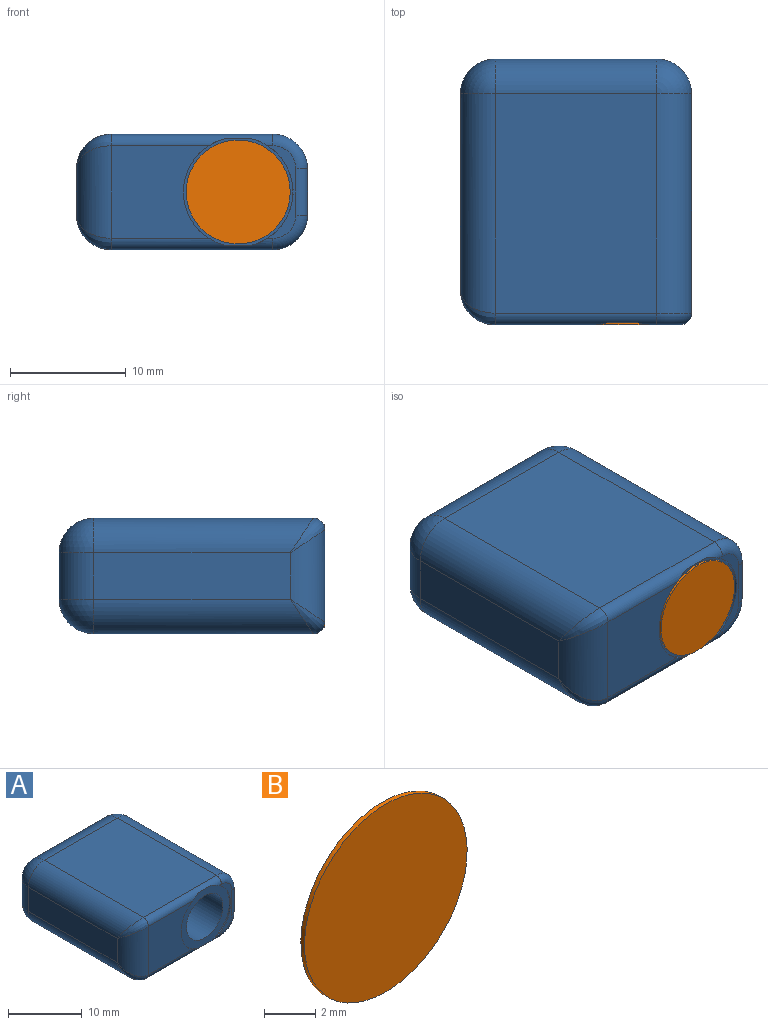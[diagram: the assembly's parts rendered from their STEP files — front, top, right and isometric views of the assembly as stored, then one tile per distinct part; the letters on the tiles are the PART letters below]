
ASSEMBLY  parts=2 mates=1
PART A: 34 faces, bbox 20.2x23x10.5 mm
  f0: cylinder r=4.75mm len=9.2mm, axis (0,-1,0), area 2.2mm2, adj f7,f9,f26,f30
  f1: plane 8.44x8mm, normal (0,-1,0), area 55.2mm2, adj f8,f23,f26,f30
  f2: plane 19x14mm, normal (0,0,1), area 266mm2, adj f15,f20,f24,f30
  f3: plane 17x4mm, normal (-1,0,0), area 68mm2, adj f19,f21,f23,f24
  f4: plane 19x14mm, normal (0,0,-1), area 266mm2, adj f12,f16,f21,f26
  f5: plane 19x4mm, normal (1,0,0), area 76mm2, adj f12,f14,f15,f28
  f6: plane 14x4mm, normal (0,1,0), area 48.9mm2, adj f14,f16,f19,f20,f32
  f7: plane 8x2.44mm, normal (0,-1,0), area 5.4mm2, adj f0,f26,f27,f28,f29,f30
  f8: cylinder r=4.75mm len=9.2mm, axis (0,-1,0), area 2.2mm2, adj f1,f9,f26,f30
  f9: plane 9.5x9.2mm, normal (0,-1,0), area 31.9mm2, adj f0,f8,f10,f26,f30
  f10: cylinder r=3.5mm len=10mm, axis (0,-1,0), area 219.9mm2, adj f9,f11
  f11: plane 7x7mm, normal (0,-1,0), area 38.5mm2, adj f10
  f12: cylinder r=3mm len=19mm, axis (0,1,0), area 89.5mm2, adj f4,f5,f13,f27
  f13: sphere r=3mm, area 14.1mm2, adj f12,f14,f16
  f14: cylinder r=3mm len=4mm, axis (0,0,-1), area 18.8mm2, adj f5,f6,f13,f17
  f15: cylinder r=3mm len=19mm, axis (0,-1,0), area 89.5mm2, adj f2,f5,f17,f29
  f16: cylinder r=3mm len=14mm, axis (-1,0,0), area 66mm2, adj f4,f6,f13,f18
  f17: sphere r=3mm, area 14.1mm2, adj f14,f15,f20
  f18: sphere r=3mm, area 14.1mm2, adj f16,f19,f21
  f19: cylinder r=3mm len=4mm, axis (0,0,1), area 18.8mm2, adj f3,f6,f18,f22
  f20: cylinder r=3mm len=14mm, axis (1,0,0), area 66mm2, adj f2,f6,f17,f22
  f21: cylinder r=3mm len=19mm, axis (0,-1,0), area 86.1mm2, adj f3,f4,f18,f25
  f22: sphere r=3mm, area 14.1mm2, adj f19,f20,f24
  f23: cylinder r=3mm len=8mm, axis (0,0,-1), area 30.8mm2, adj f1,f3,f25,f31
  f24: cylinder r=3mm len=19mm, axis (0,1,0), area 86.1mm2, adj f2,f3,f22,f31
  f25: bspline ~3.38x3mm, area 5mm2, adj f21,f23,f26
  f26: cylinder r=1mm len=14mm, axis (-1,0,0), area 19.6mm2, adj f0,f1,f4,f7,f8,f9,f25,f27
  f27: torus R=2mm, axis (0,-1,0), area 6.5mm2, adj f7,f12,f26,f28
  f28: cylinder r=1mm len=4mm, axis (0,0,1), area 6.3mm2, adj f5,f7,f27,f29
  f29: torus R=2mm, axis (0,-1,0), area 6.5mm2, adj f7,f15,f28,f30
  f30: cylinder r=1mm len=14mm, axis (1,0,0), area 19.6mm2, adj f0,f1,f2,f7,f8,f9,f29,f31
  f31: bspline ~3.38x3mm, area 5mm2, adj f23,f24,f30
  f32: cylinder r=1.5mm len=10mm, axis (0,1,0), area 94.2mm2, adj f6,f33
  f33: plane 3x3mm, normal (0,1,0), area 7.1mm2, adj f32
PART B: 3 faces, bbox 9x0.2x9 mm
  f0: cylinder r=4.5mm len=9mm, axis (0,-1,0), area 5.7mm2, adj f1,f2
  f1: plane 9x9mm, normal (0,1,0), area 63.6mm2, adj f0
  f2: plane 9x9mm, normal (0,-1,0), area 63.6mm2, adj f0
PLACE A at identity
PLACE B t=(-0.02,10,0)mm
MATE fastened B.f0 <-> A.f0  axis (0,1,0) through (4,0.2,0)mm
